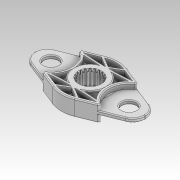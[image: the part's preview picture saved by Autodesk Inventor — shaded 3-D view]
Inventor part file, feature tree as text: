
AUTODESK INVENTOR PART (.ipt)
format: ipt  version: 2020 (Build 240168000, 168)  size: 1,332,736 bytes
history: native  units: mm
features: sketch x10, extrude x8, other x7, fillet x4, revolve x3, pattern_circular x1, imported_body x1, projected_geometry x1
ambient origin geometry x8: Origin, YZ Plane, XZ Plane, XY Plane, X Axis, Y Axis, Z Axis, Center Point
bodies: Solid1 (feature_tree)
feature tree (35):
  other  "HD_mastersketch.ipt"
  other  "Blocks"
  revolve  "Revolution1"  [1 undecoded]
  extrude  "Extrusion1"  Depth=5.0mm
  extrude  "Extrusion2"  TaperAngle=0.0deg  [1 undecoded]
  fillet  "Fillet1"  [1 undecoded]
  extrude  "Extrusion7"  Depth=12.6mm
  extrude  "Extrusion10"  TaperAngle=0.0deg  [1 undecoded]
  pattern_circular  "Circular Pattern1"  [2 undecoded]
  revolve  "Revolution3"  [1 undecoded]
  extrude  "Extrusion12"  Depth=1.0mm TaperAngle=0.0deg
  fillet  "Fillet7"  Radius=200.0mm
  fillet  "Fillet5"  Radius=0.2mm
  fillet  "Fillet6"  [1 undecoded]
  revolve  "Revolution4"  [1 undecoded]
  extrude  "Extrusion13"  Depth=1.0mm
  extrude  "Extrusion8"  Depth=1.0mm
  extrude  "Extrusion9"  Depth=1.0mm
  other  "608 bearing"
  other  "Belt"
  other  "Rotor"
  imported_body  "Base"
  sketch  "Sketch8"  dims[d1=10.0mm d24=7.0mm d25=22.0mm d26=8.0mm]
  sketch  "Sketch9"  dims[d2=90.0deg d3=5.0mm d4=10.0mm]
  sketch  "Sketch15"  dims[d5=15.0mm d6=0.0mm d7=0.0mm d8=0.0mm d9=0.0mm]
  sketch  "Sketch16"  dims[d10=7.0mm d44=12.6mm]
  sketch  "Sketch17"  dims[d45=10.0mm d46=0.0mm d47=0.0mm d48=0.0mm]
  sketch  "Sketch18"  dims[d49=4.5mm d50=0.0mm]
  sketch  "Sketch19"  dims[d51=8.726646mm]
  sketch  "Sketch20"  dims[d52=1.0mm]
  sketch  "Sketch22"  dims[d53=90.0deg]
  projected_geometry  "Projected Loop2"
  sketch  "Sketch23"  dims[d54=0.5mm d55=0.75mm d56=10.9mm d58=4.5mm d59=0.0mm d60=200.0mm d61=360.0deg d63=0.2mm d78=90.0deg d82=12.6mm d84=24.0mm d88=1.5mm d89=23.0mm d90=1.5mm d91=10.0mm d92=0.0mm d93=1.0mm d94=1.0mm d95=4.1mm d96=6.0mm d97=2.0mm d98=45.0deg d99=0.8mm d100=2.0mm d101=0.5mm d102=0.5mm d103=1.0mm d104=10.0mm d105=0.0mm]
  other  "608 bearing:1"
  other  "608 bearing:2"
note: 9 required parameter values undecoded (feature->parameter linkage not recoverable at this tier; creation-order binding heuristic only, values carry confidence <= 0.55)